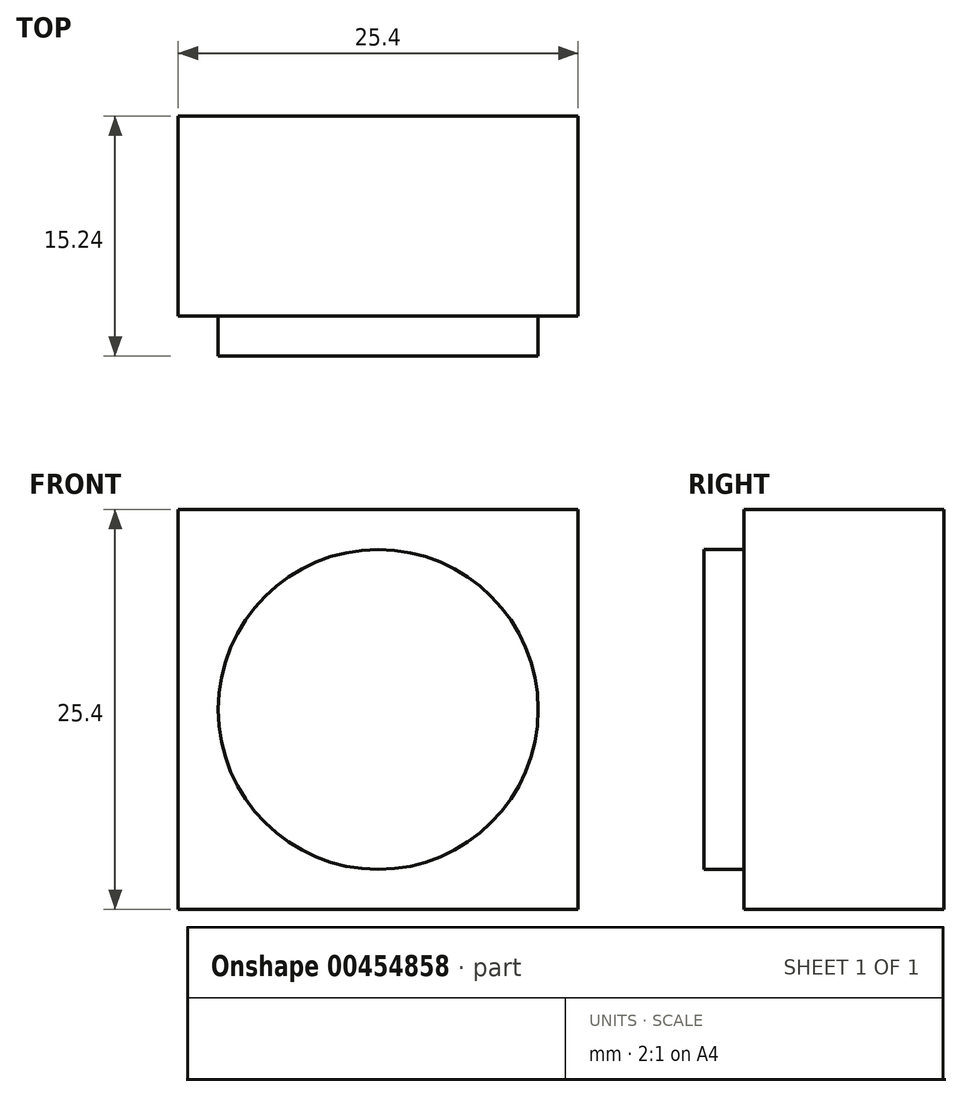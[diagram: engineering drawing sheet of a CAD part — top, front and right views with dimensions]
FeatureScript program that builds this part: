
annotation { "Feature Type Name" : "Feature", "Feature Type Description" : "" }
export const myFeature = defineFeature(function(context is Context, id is Id, definition is map)
    precondition{}
    {
        {
            var Q0;
            Q0=qCreatedBy(makeId("Front.planeOp"),FACE);
            var sketch = newSketch(context, id + "F0", { "sketchPlane" : qUnion([Q0])});
            skLineSegment(sketch, "E0.bottom", {"start": v(-6.35, 12.7) * mm, "end": v(6.35, 12.7) * mm});
            skLineSegment(sketch, "E0.top", {"start": v(-6.35, -12.7) * mm, "end": v(6.35, -12.7) * mm});
            skLineSegment(sketch, "E0.left", {"start": v(-6.35, 12.7) * mm, "end": v(-6.35, -12.7) * mm});
            skLineSegment(sketch, "E0.right", {"start": v(6.35, 12.7) * mm, "end": v(6.35, -12.7) * mm});
            skPoint(sketch, "E0.middle", {"position": v(0, 0) * mm});
            skLineSegment(sketch, "E1.bottom", {"start": v(-6.35, 12.7) * mm, "end": v(-19.05, 12.7) * mm});
            skLineSegment(sketch, "E1.top", {"start": v(-6.35, -12.7) * mm, "end": v(-19.05, -12.7) * mm});
            skLineSegment(sketch, "E1.right", {"start": v(-19.05, 12.7) * mm, "end": v(-19.05, -12.7) * mm});
            skSolve(sketch);
        }
        {
            var Q0;
            Q0=makeQuery(id+"F0.imprint","IMPRINT",FACE,{"disambiguationData":[TD([[makeQuery(id+"F0.imprint","IMPRINT",EDGE,{"derivedFrom":sQuery(id+"F0.wireOp",EDGE,"E0.bottom")}),-1.0]])]});
            extrude(context, id + "F1", {"entities" : qUnion([Q0]), "endBound" : BoundingType.SYMMETRIC, "depth" : 12.7 * mm, "offsetDistance" : 25.4 * mm});
        }
        {
            var Q0;
            Q0=makeQuery(id+"F0.imprint","IMPRINT",FACE,{"disambiguationData":[TD([[makeQuery(id+"F0.imprint","IMPRINT",EDGE,{"derivedFrom":sQuery(id+"F0.wireOp",EDGE,"E1.bottom")}),1.0]])]});
            extrude(context, id + "F2", {"entities" : qUnion([Q0]), "operationType" : NewBodyOperationType.ADD, "endBound" : BoundingType.SYMMETRIC, "depth" : 12.7 * mm, "offsetDistance" : 25.4 * mm});
        }
        {
            var Q0;
            {var subQ0=sQuery(id+"F0.wireOp",EDGE,"E0.left");Q0=makeQuery(id+"F2.boolean.opBoolean","MERGE",FACE,{"derivedFrom":[makeQuery(id+"F1.opExtrude","CAP_FACE",FACE,{"disambiguationData":[OSD([sQuery(id+"F0.wireOp",EDGE,"E0.bottom"),sQuery(id+"F0.wireOp",EDGE,"E0.top"),sQuery(id+"F0.wireOp",EDGE,"E0.right"),subQ0])],"isStart":false}),makeQuery(id+"F2.opExtrude","CAP_FACE",FACE,{"disambiguationData":[OSD([sQuery(id+"F0.wireOp",EDGE,"E1.bottom"),sQuery(id+"F0.wireOp",EDGE,"E1.top"),subQ0,sQuery(id+"F0.wireOp",EDGE,"E1.right")])],"isStart":false})]});}
            var sketch = newSketch(context, id + "F3", { "sketchPlane" : qUnion([Q0])});
            skCircle(sketch, "E2", {"center": v(-6.35, 0) * mm, "radius": 10.16 * mm});
            skPoint(sketch, "E2.centerSnap0", {"position": v(-6.35, 12.7) * mm});
            skSolve(sketch);
        }
        {
            var Q0;
            Q0=makeQuery(id+"F3.imprint","IMPRINT",FACE,{"disambiguationData":[TD([[makeQuery(id+"F3.imprint","IMPRINT",EDGE,{"derivedFrom":sQuery(id+"F3.wireOp",EDGE,"E2")}),1.0]])]});
            extrude(context, id + "F4", {"entities" : qUnion([Q0]), "operationType" : NewBodyOperationType.ADD, "depth" : 2.54 * mm, "offsetDistance" : 25.4 * mm});
        }
    });
